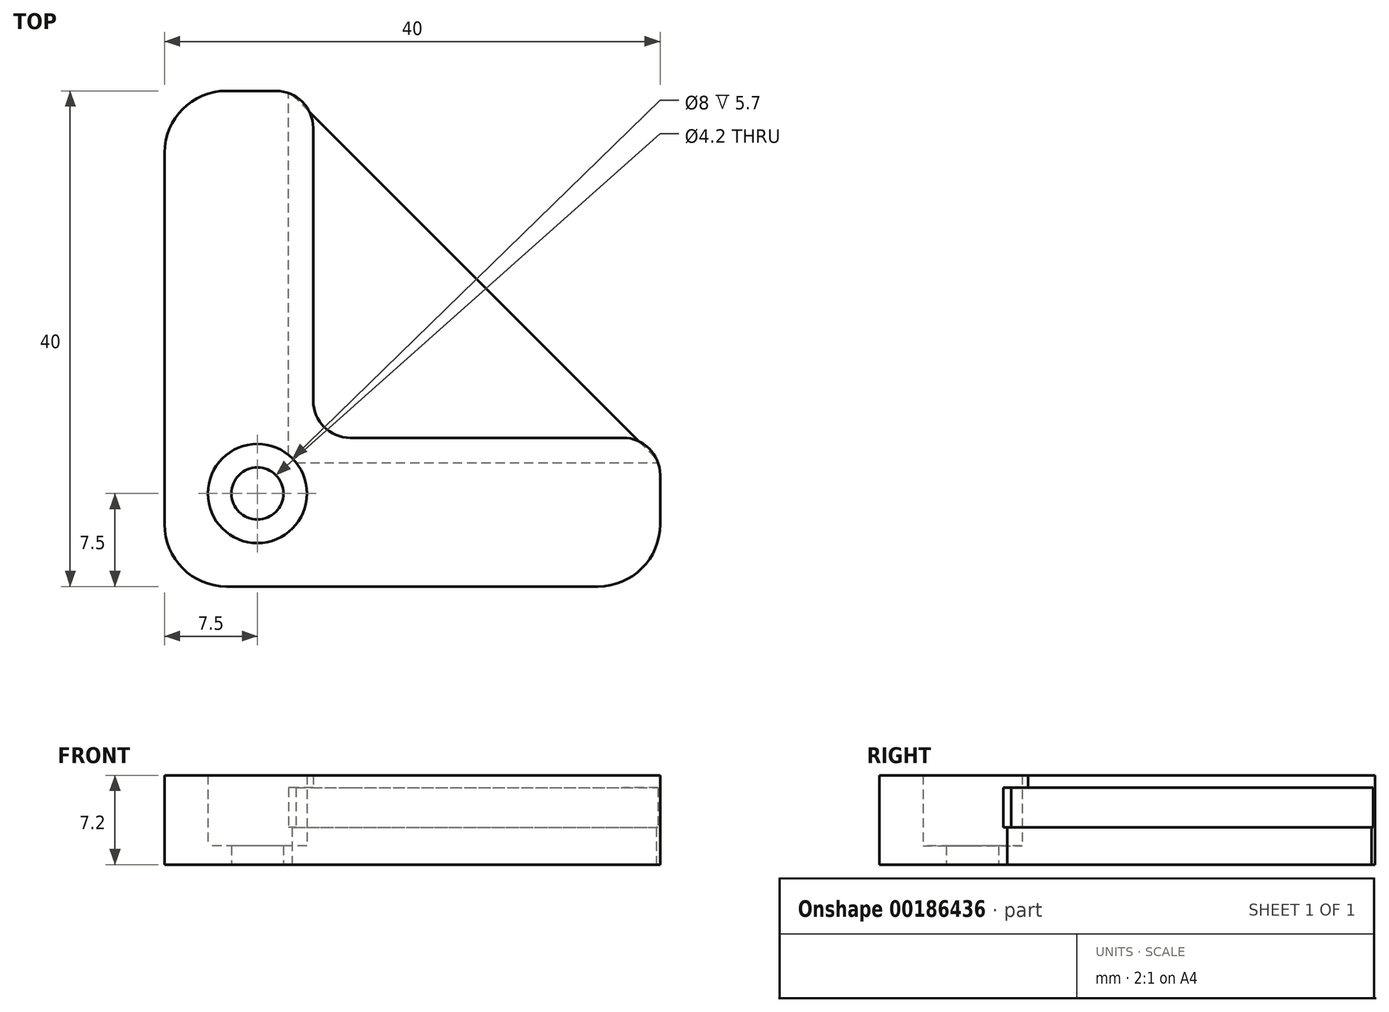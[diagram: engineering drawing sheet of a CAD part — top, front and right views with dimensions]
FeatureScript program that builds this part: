
annotation { "Feature Type Name" : "Feature", "Feature Type Description" : "" }
export const myFeature = defineFeature(function(context is Context, id is Id, definition is map)
    precondition{}
    {
        {
            var Q0;
            Q0=qCreatedBy(makeId("Top.planeOp"),FACE);
            var sketch = newSketch(context, id + "F0", { "sketchPlane" : qUnion([Q0])});
            skLineSegment(sketch, "E0", {"start": v(0, 0) * mm, "end": v(0, 40) * mm});
            skLineSegment(sketch, "E1", {"start": v(0, 0) * mm, "end": v(40, 0) * mm});
            skLineSegment(sketch, "E2.0", {"start": v(10, 10.62) * mm, "end": v(10, 40) * mm});
            skLineSegment(sketch, "E3.0", {"start": v(10.62, 10) * mm, "end": v(40, 10) * mm});
            skLineSegment(sketch, "E4", {"start": v(10, 40) * mm, "end": v(0, 40) * mm});
            skLineSegment(sketch, "E5", {"start": v(40, 10) * mm, "end": v(40, 0) * mm});
            skCircle(sketch, "E6", {"center": v(7.5, 7.5) * mm, "radius": 2.1 * mm});
            skLineSegment(sketch, "E7", {"start": v(10, 40) * mm, "end": v(40, 10) * mm});
            skCircle(sketch, "E8", {"center": v(7.5, 7.5) * mm, "radius": 4 * mm});
            skSolve(sketch);
        }
        {
            var Q0;
            Q0=makeQuery(id+"F0.imprint","IMPRINT",FACE,{"disambiguationData":[TD([[makeQuery(id+"F0.imprint","IMPRINT",EDGE,{"derivedFrom":sQuery(id+"F0.wireOp",EDGE,"E0")}),-1.0]])]});
            extrude(context, id + "F1", {"entities" : qUnion([Q0]), "depth" : 6.2 * mm, "offsetDistance" : 25 * mm});
        }
        {
            var Q0;
            Q0=makeQuery(id+"F0.imprint","IMPRINT",FACE,{"disambiguationData":[TD([[makeQuery(id+"F0.imprint","IMPRINT",EDGE,{"derivedFrom":sQuery(id+"F0.wireOp",EDGE,"E6")}),-1.0]])]});
            extrude(context, id + "F2", {"entities" : qUnion([Q0]), "operationType" : NewBodyOperationType.ADD, "depth" : 1.5 * mm});
        }
        {
            var Q0;
            {var subQ0=sQuery(id+"F0.wireOp",EDGE,"E2.0");Q0=makeQuery(id+"F0.imprint","IMPRINT",FACE,{"disambiguationData":[TD([[makeQuery(id+"F0.imprint","IMPRINT",EDGE,{"derivedFrom":subQ0}),-1.0]])]});}
            extrude(context, id + "F3", {"entities" : qUnion([Q0]), "operationType" : NewBodyOperationType.ADD, "depth" : 3 * mm});
        }
        {
            var Q0;
            Q0=makeQuery(id+"F1.opExtrude","CAP_FACE",FACE,{"disambiguationData":[OSD([sQuery(id+"F0.wireOp",EDGE,"E0"),sQuery(id+"F0.wireOp",EDGE,"E1"),sQuery(id+"F0.wireOp",EDGE,"E2.0"),sQuery(id+"F0.wireOp",EDGE,"E3.0"),sQuery(id+"F0.wireOp",EDGE,"E4"),sQuery(id+"F0.wireOp",EDGE,"E5"),sQuery(id+"F0.wireOp",EDGE,"E8")])],"isStart":false});
            var sketch = newSketch(context, id + "F4", { "sketchPlane" : qUnion([Q0])});
            skLineSegment(sketch, "E9.bottom", {"start": v(0, 0) * mm, "end": v(12, 0) * mm});
            skLineSegment(sketch, "E9.top", {"start": v(0, 40) * mm, "end": v(12, 40) * mm});
            skLineSegment(sketch, "E9.left", {"start": v(0, 0) * mm, "end": v(0, 40) * mm});
            skLineSegment(sketch, "E9.right", {"start": v(12, 12) * mm, "end": v(12, 40) * mm});
            skLineSegment(sketch, "E10.bottom", {"start": v(0, 0) * mm, "end": v(40, 0) * mm});
            skLineSegment(sketch, "E10.top", {"start": v(12, 12) * mm, "end": v(40, 12) * mm});
            skLineSegment(sketch, "E10.left", {"start": v(0, 0) * mm, "end": v(0, 12) * mm});
            skLineSegment(sketch, "E10.right", {"start": v(40, 0) * mm, "end": v(40, 12) * mm});
            skCircle(sketch, "E11", {"center": v(7.5, 7.5) * mm, "radius": 4 * mm});
            skSolve(sketch);
        }
        {
            var Q0;
            {var subQ4=sQuery(id+"F4.wireOp",EDGE,"E9.left");Q0=makeQuery(id+"F4.imprint","IMPRINT",FACE,{"disambiguationData":[TD([[makeQuery(id+"F4.imprint","IMPRINT",EDGE,{"derivedFrom":subQ4}),-1.0]])]});}
            var Q1;
            {var subQ3=sQuery(id+"F4.wireOp",EDGE,"E9.right");Q1=makeQuery(id+"F4.imprint","IMPRINT",FACE,{"disambiguationData":[TD([[makeQuery(id+"F4.imprint","IMPRINT",EDGE,{"derivedFrom":subQ3}),1.0]])]});}
            extrude(context, id + "F5", {"entities" : qUnion([Q0, Q1]), "operationType" : NewBodyOperationType.ADD, "depth" : 1 * mm, "offsetDistance" : 25 * mm});
        }
        {
            var Q0;
            Q0=makeQuery(id+"F5.boolean.opBoolean","MERGE",EDGE,{"derivedFrom":[makeQuery(id+"F1.opExtrude","SWEPT_EDGE",EDGE,{"disambiguationData":[OSD([sQuery(id+"F0.wireOp",EDGE,"E0"),sQuery(id+"F0.wireOp",EDGE,"E4")])]}),makeQuery(id+"F5.opExtrude","SWEPT_EDGE",EDGE,{"disambiguationData":[OSD([sQuery(id+"F4.wireOp",EDGE,"E9.top"),sQuery(id+"F4.wireOp",EDGE,"E9.left")])]})]});
            var Q1;
            Q1=makeQuery(id+"F5.boolean.opBoolean","MERGE",EDGE,{"derivedFrom":[makeQuery(id+"F1.opExtrude","SWEPT_EDGE",EDGE,{"disambiguationData":[OSD([sQuery(id+"F0.wireOp",EDGE,"E0"),sQuery(id+"F0.wireOp",EDGE,"E1")])]}),makeQuery(id+"F5.opExtrude","SWEPT_EDGE",EDGE,{"disambiguationData":[OSD([sQuery(id+"F4.wireOp",EDGE,"E10.bottom"),sQuery(id+"F4.wireOp",EDGE,"E10.left")])]})]});
            var Q2;
            Q2=makeQuery(id+"F5.boolean.opBoolean","MERGE",EDGE,{"derivedFrom":[makeQuery(id+"F1.opExtrude","SWEPT_EDGE",EDGE,{"disambiguationData":[OSD([sQuery(id+"F0.wireOp",EDGE,"E1"),sQuery(id+"F0.wireOp",EDGE,"E5")])]}),makeQuery(id+"F5.opExtrude","SWEPT_EDGE",EDGE,{"disambiguationData":[OSD([sQuery(id+"F4.wireOp",EDGE,"E10.bottom"),sQuery(id+"F4.wireOp",EDGE,"E10.right")])]})]});
            fillet(context, id + "F6", {"entities" : qUnion([Q0, Q1, Q2]), "radius" : 5 * mm, "tangentPropagation" : true, "allowEdgeOverflow" : false});
        }
        {
            var Q0;
            Q0=makeQuery(id+"F5.opExtrude","SWEPT_EDGE",EDGE,{"disambiguationData":[OSD([sQuery(id+"F4.wireOp",EDGE,"E9.top"),sQuery(id+"F4.wireOp",EDGE,"E9.right")])]});
            var Q1;
            Q1=makeQuery(id+"F5.opExtrude","SWEPT_EDGE",EDGE,{"disambiguationData":[OSD([sQuery(id+"F4.wireOp",EDGE,"E10.top"),sQuery(id+"F4.wireOp",EDGE,"E10.right")])]});
            fillet(context, id + "F7", {"entities" : qUnion([Q0, Q1]), "radius" : 3 * mm, "tangentPropagation" : true, "allowEdgeOverflow" : false});
        }
        {
            var Q0;
            Q0=makeQuery(id+"F5.opExtrude","SWEPT_EDGE",EDGE,{"disambiguationData":[OSD([sQuery(id+"F4.wireOp",EDGE,"E9.right"),sQuery(id+"F4.wireOp",EDGE,"E10.top")])]});
            fillet(context, id + "F8", {"entities" : qUnion([Q0]), "radius" : 3 * mm, "tangentPropagation" : true, "allowEdgeOverflow" : false});
        }
    });
